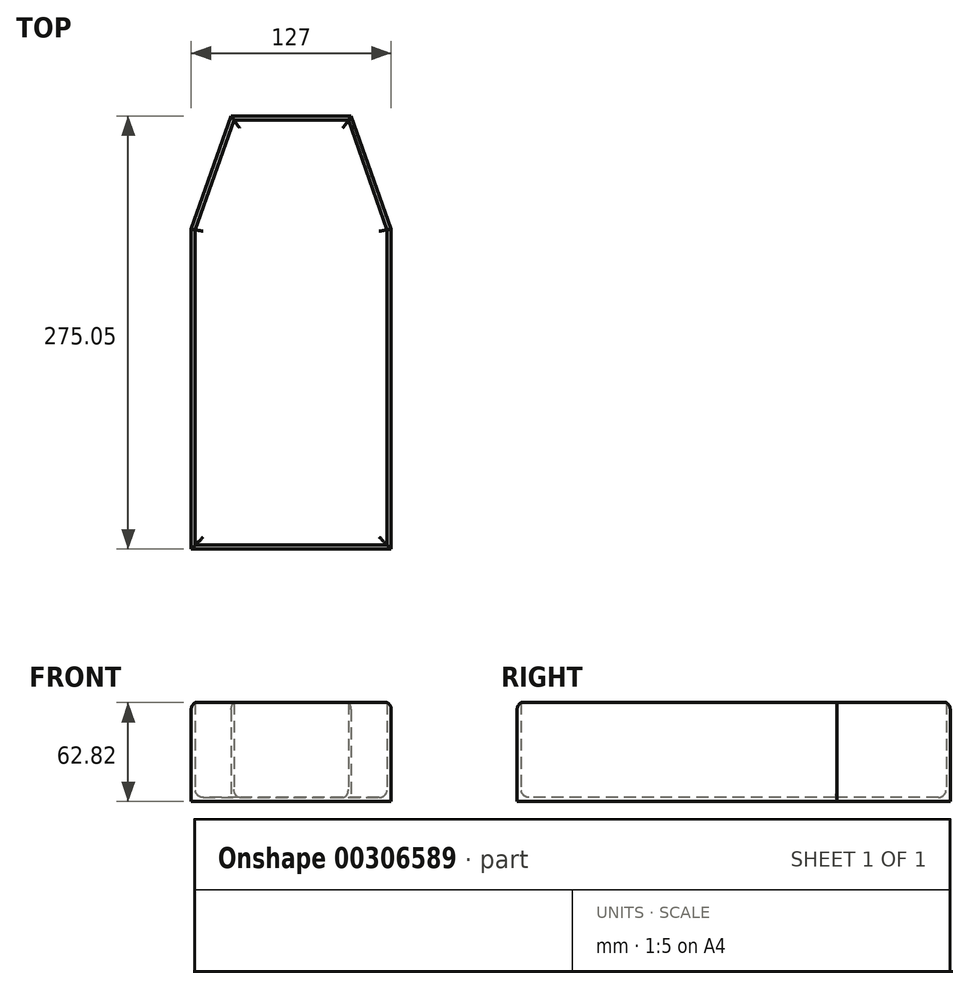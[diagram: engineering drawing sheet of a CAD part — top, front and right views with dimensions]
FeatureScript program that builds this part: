
annotation { "Feature Type Name" : "Feature", "Feature Type Description" : "" }
export const myFeature = defineFeature(function(context is Context, id is Id, definition is map)
    precondition{}
    {
        {
            var Q0;
            Q0=qCreatedBy(makeId("Top.planeOp"),FACE);
            var sketch = newSketch(context, id + "F0", { "sketchPlane" : qUnion([Q0])});
            skLineSegment(sketch, "E0", {"start": v(-57.62, 55.71) * mm, "end": v(-57.62, -147.49) * mm});
            skLineSegment(sketch, "E1", {"start": v(-57.62, -147.49) * mm, "end": v(69.38, -147.49) * mm});
            skLineSegment(sketch, "E2", {"start": v(69.38, -147.49) * mm, "end": v(69.38, 55.71) * mm});
            skLineSegment(sketch, "E3", {"start": v(69.38, 55.71) * mm, "end": v(43.98, 127.56) * mm});
            skLineSegment(sketch, "E4", {"start": v(43.98, 127.56) * mm, "end": v(-32.22, 127.56) * mm});
            skLineSegment(sketch, "E5", {"start": v(-32.22, 127.56) * mm, "end": v(-57.62, 55.71) * mm});
            skSolve(sketch);
        }
        {
            var Q0;
            Q0 = qSketchRegion(id + "F0", true);
            extrude(context, id + "F1", {"entities" : qUnion([Q0]), "depth" : 63.5 * mm});
        }
        {
            var Q0;
            Q0=makeQuery(id+"F1.opExtrude","CAP_FACE",FACE,{"disambiguationData":[OSD([sQuery(id+"F0.wireOp",EDGE,"E0"),sQuery(id+"F0.wireOp",EDGE,"E1"),sQuery(id+"F0.wireOp",EDGE,"E2"),sQuery(id+"F0.wireOp",EDGE,"E3"),sQuery(id+"F0.wireOp",EDGE,"E4"),sQuery(id+"F0.wireOp",EDGE,"E5")])],"isStart":false});
            shell(context, id + "F2", {"entities" : qUnion([Q0]), "thickness" : 2.54 * mm});
        }
        {
            var Q0;
            Q0=makeQuery(id+"F2.opShell","OFFSET_FACE",FACE,{"disambiguationData":[OSD([sQuery(id+"F0.wireOp",EDGE,"E0"),sQuery(id+"F0.wireOp",EDGE,"E1"),sQuery(id+"F0.wireOp",EDGE,"E2"),sQuery(id+"F0.wireOp",EDGE,"E3"),sQuery(id+"F0.wireOp",EDGE,"E4"),sQuery(id+"F0.wireOp",EDGE,"E5")])]});
            fillet(context, id + "F3", {"entities" : qUnion([Q0]), "radius" : 5.08 * mm, "tangentPropagation" : true, "allowEdgeOverflow" : false});
        }
        {
            var Q0;
            Q0=makeQuery(id+"F1.opExtrude","CAP_EDGE",EDGE,{"disambiguationData":[OSD([sQuery(id+"F0.wireOp",EDGE,"E5")])],"isStart":false});
            var Q1;
            Q1=makeQuery(id+"F1.opExtrude","CAP_EDGE",EDGE,{"disambiguationData":[OSD([sQuery(id+"F0.wireOp",EDGE,"E4")])],"isStart":false});
            var Q2;
            Q2=makeQuery(id+"F1.opExtrude","CAP_EDGE",EDGE,{"disambiguationData":[OSD([sQuery(id+"F0.wireOp",EDGE,"E3")])],"isStart":false});
            var Q3;
            Q3=makeQuery(id+"F1.opExtrude","CAP_EDGE",EDGE,{"disambiguationData":[OSD([sQuery(id+"F0.wireOp",EDGE,"E0")])],"isStart":false});
            var Q4;
            Q4=makeQuery(id+"F1.opExtrude","CAP_EDGE",EDGE,{"disambiguationData":[OSD([sQuery(id+"F0.wireOp",EDGE,"E2")])],"isStart":false});
            var Q5;
            Q5=makeQuery(id+"F1.opExtrude","CAP_EDGE",EDGE,{"disambiguationData":[OSD([sQuery(id+"F0.wireOp",EDGE,"E1")])],"isStart":false});
            fillet(context, id + "F4", {"entities" : qUnion([Q0, Q1, Q2, Q3, Q4, Q5]), "radius" : 5.08 * mm, "tangentPropagation" : true, "allowEdgeOverflow" : false});
        }
    });
